# Revit family: Windows_Roof-Windows_Lamilux_F100G_Round
name_source: partatom
category: Windows
revit_build: Autodesk Revit 2014 (Build: 20130308_1515(x64)
units: mm (PartAtom-declared; Revit-internal decimal feet)

## types (21) — shared parameters
Analytic Construction = <None>
BIMobject category = Roof Windows
Brand url = http://www.lamilux.com
Design country = Germany
Edition number = 1
IFC Classification = Window
Main Material = Lamilux-White
Manufacturer country = Germany
Manufacturer name = LAMILUX
Material main = Glass
Material secondary = Plastic
NBS Reference Code = 20-30-74
NBS Reference Description = Roof Light Systems
OmniClass Code = 23-17 17 00
OmniClass Description = Skylights
Opening Types Option 1 = Opening Type : Air Opening
Opening types = Ventilable, fixed
Option 1 = Glazing : Double thermal insulation glazing-clear film
Option 2 = Glazing : Double thermal insulation glazing-matt film
Option 3 = Glazing : Triple thermal insulation glass-clear film
Option 4 = Glazing : Triple thermal insulation glass-matt film
Product Guid = 6c46bdb6-9118-4e00-a0b6-b4321a2f367e
Product SKU = Lamilux_F100G_round
Product data url = https://bimobject.com
Product family = Daylight element
Product group = Flat roof window
Product url = http://www.lamilux.com
QR code = http://bimobject.com
Secondary Material = Lamilux- Glass
UNSPSC Code = 301516
Uniclass 1.4 Code = JL11
Uniclass 1.4 Description = Rooflights/Roof windows
Uniclass 2.0 Code = SS-20-30-74
Uniclass 2.0 Description = Roof Light Systems
Uniclass 2015 Code = Ss_30_30_34
Uniclass 2015 Name = Glass unit masonry roof light systems
zero-valued in all types: Nominal height, Nominal width, Weight Net (Kg)

## per-type parameters (varying)
| type | Double Operator Distance | Height | Internal Radius | Rough Height | Width |
| 60x30 | 590 mm  [stored 1.9357 ft] | 300 mm  [stored 0.984252 ft] | 300 mm  [stored 0.984252 ft] | 300 mm  [stored 0.984252 ft] | 600 mm |
| 150x50 | 600 mm | 500 mm  [stored 1.64042 ft] | 750 mm  [stored 2.46063 ft] | 500 mm  [stored 1.64042 ft] | 1500 mm  [stored 4.92126 ft] |
| 80x30 | 590 mm  [stored 1.9357 ft] | 300 mm  [stored 0.984252 ft] | 400 mm  [stored 1.31234 ft] | 300 mm  [stored 0.984252 ft] | 800 mm  [stored 2.62467 ft] |
| 100x30 | 590 mm  [stored 1.9357 ft] | 300 mm  [stored 0.984252 ft] | 500 mm  [stored 1.64042 ft] | 300 mm  [stored 0.984252 ft] | 1000 mm  [stored 3.28084 ft] |
| 90x30 | 590 mm  [stored 1.9357 ft] | 300 mm  [stored 0.984252 ft] | 450 mm  [stored 1.47638 ft] | 300 mm  [stored 0.984252 ft] | 900 mm  [stored 2.95276 ft] |
| 120x30 | 590 mm  [stored 1.9357 ft] | 300 mm  [stored 0.984252 ft] | 600 mm | 300 mm  [stored 0.984252 ft] | 1200 mm |
| 150x30 | 610 mm  [stored 2.00131 ft] | 300 mm  [stored 0.984252 ft] | 750 mm  [stored 2.46063 ft] | 300 mm  [stored 0.984252 ft] | 1500 mm  [stored 4.92126 ft] |
| 180x30 | 760 mm | 300 mm  [stored 0.984252 ft] | 900 mm  [stored 2.95276 ft] | 300 mm  [stored 0.984252 ft] | 1800 mm  [stored 5.90551 ft] |
| 60x50 | 590 mm  [stored 1.9357 ft] | 500 mm  [stored 1.64042 ft] | 300 mm  [stored 0.984252 ft] | 500 mm  [stored 1.64042 ft] | 600 mm |
| 80x50 | 590 mm  [stored 1.9357 ft] | 500 mm  [stored 1.64042 ft] | 400 mm  [stored 1.31234 ft] | 500 mm  [stored 1.64042 ft] | 800 mm  [stored 2.62467 ft] |
| 90x50 | 590 mm  [stored 1.9357 ft] | 500 mm  [stored 1.64042 ft] | 450 mm  [stored 1.47638 ft] | 500 mm  [stored 1.64042 ft] | 900 mm  [stored 2.95276 ft] |
| 100x50 | 590 mm  [stored 1.9357 ft] | 500 mm  [stored 1.64042 ft] | 500 mm  [stored 1.64042 ft] | 500 mm  [stored 1.64042 ft] | 1000 mm  [stored 3.28084 ft] |
| 120x50 | 590 mm  [stored 1.9357 ft] | 500 mm  [stored 1.64042 ft] | 600 mm | 500 mm  [stored 1.64042 ft] | 1200 mm |
| 180x50 | 750 mm  [stored 2.46063 ft] | 500 mm  [stored 1.64042 ft] | 900 mm  [stored 2.95276 ft] | 500 mm  [stored 1.64042 ft] | 1800 mm  [stored 5.90551 ft] |
| 60x70 | 590 mm  [stored 1.9357 ft] | 700 mm  [stored 2.29659 ft] | 300 mm  [stored 0.984252 ft] | 700 mm  [stored 2.29659 ft] | 600 mm |
| 80x70 | 590 mm  [stored 1.9357 ft] | 700 mm  [stored 2.29659 ft] | 400 mm  [stored 1.31234 ft] | 700 mm  [stored 2.29659 ft] | 800 mm  [stored 2.62467 ft] |
| 90x70 | 590 mm  [stored 1.9357 ft] | 700 mm  [stored 2.29659 ft] | 450 mm  [stored 1.47638 ft] | 700 mm  [stored 2.29659 ft] | 900 mm  [stored 2.95276 ft] |
| 100x70 | 590 mm  [stored 1.9357 ft] | 700 mm  [stored 2.29659 ft] | 500 mm  [stored 1.64042 ft] | 700 mm  [stored 2.29659 ft] | 1000 mm  [stored 3.28084 ft] |
| 120x70 | 590 mm  [stored 1.9357 ft] | 700 mm  [stored 2.29659 ft] | 600 mm | 700 mm  [stored 2.29659 ft] | 1200 mm |
| 150x70 | 590 mm  [stored 1.9357 ft] | 700 mm  [stored 2.29659 ft] | 750 mm  [stored 2.46063 ft] | 700 mm  [stored 2.29659 ft] | 1500 mm  [stored 4.92126 ft] |
| 180x70 | 740 mm  [stored 2.42782 ft] | 700 mm  [stored 2.29659 ft] | 900 mm  [stored 2.95276 ft] | 700 mm  [stored 2.29659 ft] | 1800 mm  [stored 5.90551 ft] |

note: [stored X ft] marks values corroborated as IEEE doubles in the binary element streams (Revit-internal decimal feet)

## geometry (parser evidence)
native form markers: Sweep x11
no freeform markers — native parametric forms only
